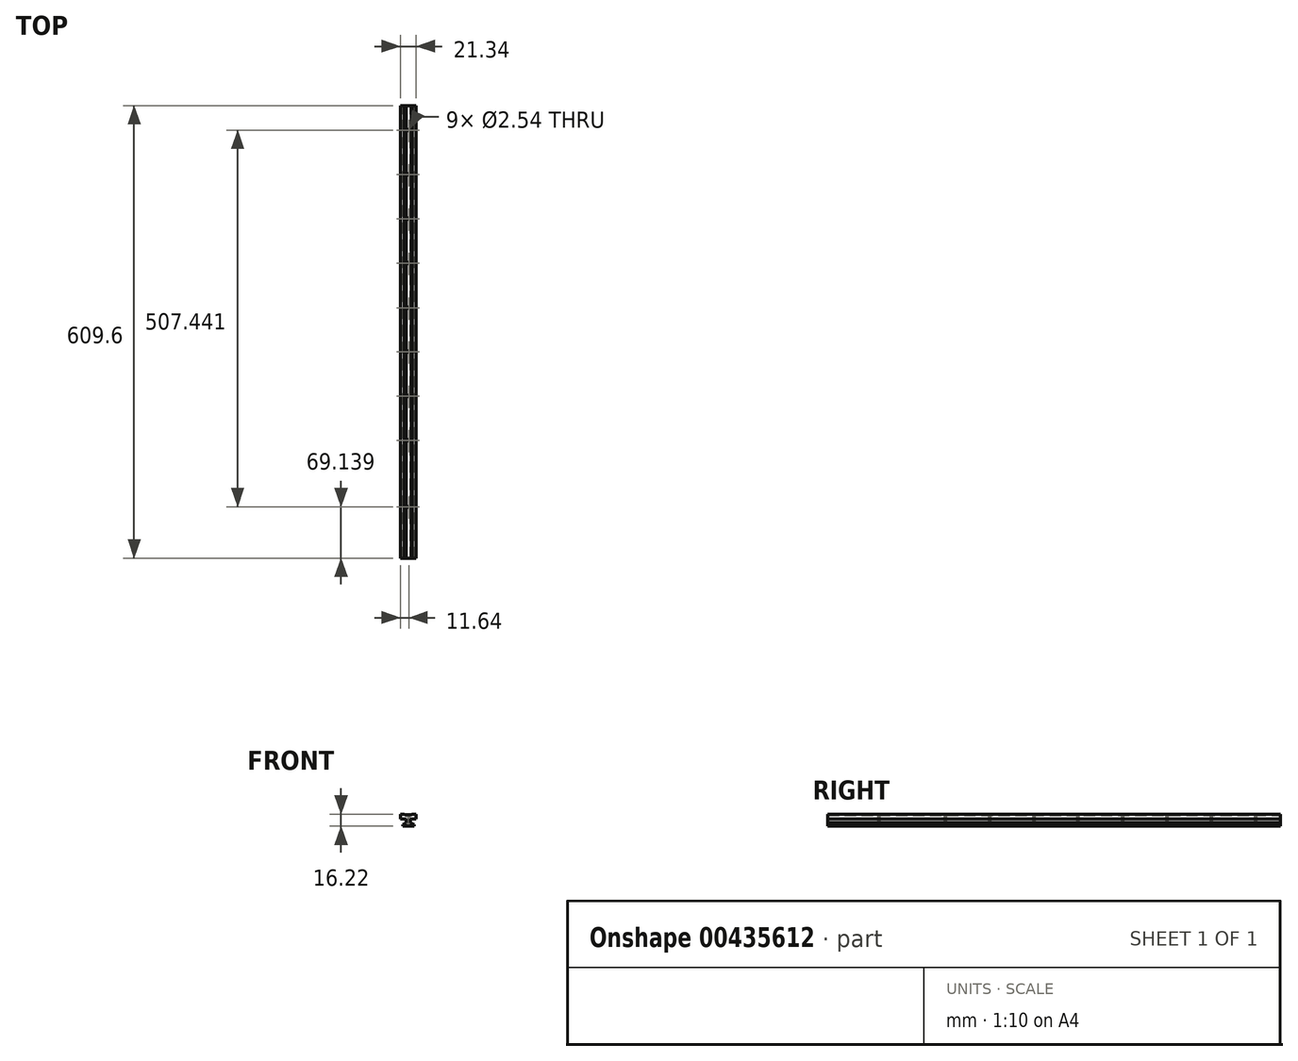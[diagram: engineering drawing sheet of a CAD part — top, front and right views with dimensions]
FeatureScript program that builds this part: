
annotation { "Feature Type Name" : "Feature", "Feature Type Description" : "" }
export const myFeature = defineFeature(function(context is Context, id is Id, definition is map)
    precondition{}
    {
        {
            var Q0;
            Q0=qCreatedBy(makeId("Front.planeOp"),FACE);
            var sketch = newSketch(context, id + "F0", { "sketchPlane" : qUnion([Q0])});
            skLineSegment(sketch, "E0", {"start": v(-11.64, -4.44) * mm, "end": v(-6.56, -4.44) * mm});
            skLineSegment(sketch, "E1", {"start": v(4.62, -4.44) * mm, "end": v(9.7, -4.44) * mm});
            skLineSegment(sketch, "E2", {"start": v(-11.64, -4.44) * mm, "end": v(-11.64, -11.04) * mm});
            skLineSegment(sketch, "E3", {"start": v(-11.64, -11.04) * mm, "end": v(-4.02, -11.04) * mm});
            skLineSegment(sketch, "E4", {"start": v(-4.02, -11.04) * mm, "end": v(-4.02, -16.12) * mm});
            skLineSegment(sketch, "E5", {"start": v(9.7, -4.44) * mm, "end": v(9.7, -11.04) * mm});
            skLineSegment(sketch, "E6", {"start": v(9.7, -11.04) * mm, "end": v(2.08, -11.04) * mm});
            skLineSegment(sketch, "E7", {"start": v(2.08, -11.04) * mm, "end": v(2.08, -16.12) * mm});
            skLineSegment(sketch, "E8", {"start": v(-4.02, -16.12) * mm, "end": v(-8.58, -18.37) * mm});
            skLineSegment(sketch, "E9", {"start": v(-8.58, -18.37) * mm, "end": v(-8.58, -20.66) * mm});
            skLineSegment(sketch, "E10", {"start": v(-8.58, -20.66) * mm, "end": v(-4.77, -20.66) * mm});
            skLineSegment(sketch, "E11", {"start": v(2.08, -16.12) * mm, "end": v(6.66, -18.3) * mm});
            skLineSegment(sketch, "E12", {"start": v(6.66, -18.3) * mm, "end": v(6.66, -20.6) * mm});
            skLineSegment(sketch, "E13", {"start": v(6.66, -20.6) * mm, "end": v(2.85, -20.6) * mm});
            skLineSegment(sketch, "E14", {"start": v(-5.42, -5.11) * mm, "end": v(3.47, -5.11) * mm});
            skLineSegment(sketch, "E15", {"start": v(-6.56, -4.44) * mm, "end": v(-5.42, -5.11) * mm});
            skLineSegment(sketch, "E16", {"start": v(3.47, -5.11) * mm, "end": v(4.62, -4.44) * mm});
            skLineSegment(sketch, "E17", {"start": v(-4.77, -20.66) * mm, "end": v(-4.16, -20.15) * mm});
            skLineSegment(sketch, "E18", {"start": v(-4.16, -20.15) * mm, "end": v(2.2, -20.15) * mm});
            skLineSegment(sketch, "E19", {"start": v(2.2, -20.15) * mm, "end": v(2.85, -20.6) * mm});
            skCircle(sketch, "E20", {"center": v(-4.15, -5.11) * mm, "radius": 0.44 * mm});
            skSolve(sketch);
        }
        {
            var Q0;
            Q0=makeQuery(id+"F0.imprint","IMPRINT",FACE,{"disambiguationData":[TD([[makeQuery(id+"F0.imprint","IMPRINT",EDGE,{"derivedFrom":sQuery(id+"F0.wireOp",EDGE,"E0")}),-1.0]])]});
            extrude(context, id + "F1", {"entities" : qUnion([Q0]), "depth" : 609.6 * mm, "offsetDistance" : 25.4 * mm});
        }
        {
            var Q0;
            {var subQ0=sQuery(id+"F0.wireOp",EDGE,"E14");Q0=makeQuery(id+"F1.opExtrude","SWEPT_FACE",FACE,{"disambiguationData":[OSD([subQ0]),TDD([makeQuery(id+"F0.imprint","IMPRINT",EDGE,{"disambiguationData":[TD([[makeQuery(id+"F0.imprint","INTERSECT",VERTEX,{"derivedFrom":[subQ0,sQuery(id+"F0.wireOp",EDGE,"E16")]}),1.0]])],"derivedFrom":subQ0})])]});}
            var sketch = newSketch(context, id + "F2", { "sketchPlane" : qUnion([Q0])});
            skPoint(sketch, "E21", {"position": v(0, -33.02) * mm});
            skPoint(sketch, "E22", {"position": v(0, -92.71) * mm});
            skPoint(sketch, "E23", {"position": v(0, -152.4) * mm});
            skPoint(sketch, "E24", {"position": v(0, -212.1) * mm});
            skPoint(sketch, "E25", {"position": v(0, -271.78) * mm});
            skPoint(sketch, "E26", {"position": v(0, -272.46) * mm});
            skPoint(sketch, "E27", {"position": v(0, -331.47) * mm});
            skPoint(sketch, "E28", {"position": v(0, -391.16) * mm});
            skPoint(sketch, "E29", {"position": v(0, -450.85) * mm});
            skPoint(sketch, "E30", {"position": v(0, -540.46) * mm});
            skSolve(sketch);
        }
        {
            var Q0;
            Q0=sQuery(id+"F2.wireOp",VERTEX,"E21");
            var Q1;
            Q1=sQuery(id+"F2.wireOp",VERTEX,"E22");
            var Q2;
            Q2=sQuery(id+"F2.wireOp",VERTEX,"E23");
            var Q3;
            Q3=sQuery(id+"F2.wireOp",VERTEX,"E24");
            var Q4;
            Q4=sQuery(id+"F2.wireOp",VERTEX,"E26");
            var Q5;
            Q5=sQuery(id+"F2.wireOp",VERTEX,"E27");
            var Q6;
            Q6=sQuery(id+"F2.wireOp",VERTEX,"E28");
            var Q7;
            Q7=sQuery(id+"F2.wireOp",VERTEX,"E29");
            var Q8;
            Q8=sQuery(id+"F2.wireOp",VERTEX,"E30");
            var Q9;
            Q9=makeQuery(id+"F1.opExtrude","SWEPT_BODY",BODY,{"disambiguationData":[OSD([sQuery(id+"F0.wireOp",EDGE,"E0"),sQuery(id+"F0.wireOp",EDGE,"E1"),sQuery(id+"F0.wireOp",EDGE,"E2"),sQuery(id+"F0.wireOp",EDGE,"E3"),sQuery(id+"F0.wireOp",EDGE,"E4"),sQuery(id+"F0.wireOp",EDGE,"E5"),sQuery(id+"F0.wireOp",EDGE,"E6"),sQuery(id+"F0.wireOp",EDGE,"E7"),sQuery(id+"F0.wireOp",EDGE,"E8"),sQuery(id+"F0.wireOp",EDGE,"E9"),sQuery(id+"F0.wireOp",EDGE,"E10"),sQuery(id+"F0.wireOp",EDGE,"E11"),sQuery(id+"F0.wireOp",EDGE,"E12"),sQuery(id+"F0.wireOp",EDGE,"E13"),sQuery(id+"F0.wireOp",EDGE,"E14"),sQuery(id+"F0.wireOp",EDGE,"E15"),sQuery(id+"F0.wireOp",EDGE,"E16"),sQuery(id+"F0.wireOp",EDGE,"E17"),sQuery(id+"F0.wireOp",EDGE,"E18"),sQuery(id+"F0.wireOp",EDGE,"E19"),sQuery(id+"F0.wireOp",EDGE,"E20")])]});
            hole(context, id + "F3", {"style" : HoleStyle.SIMPLE, "endStyle" : HoleEndStyle.THROUGH, "holeDiameter" : 2.54 * mm, "majorDiameter" : 6.35 * mm, "isTappedThrough" : true, "tappedDepth" : 12.7 * mm, "tapClearance" : 3, "locations" : qUnion([Q0, Q1, Q2, Q3, Q4, Q5, Q6, Q7, Q8]), "scope" : qUnion([Q9])});
        }
    });
